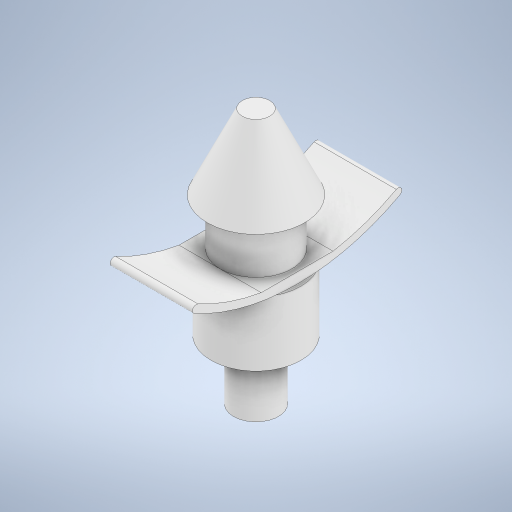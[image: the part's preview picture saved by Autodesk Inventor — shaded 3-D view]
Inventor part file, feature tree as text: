
AUTODESK INVENTOR PART (.ipt)
format: ipt  version: 2024.2 (Build 282272000, 272)  size: 308,736 bytes
history: native  units: mm
features: sketch x1, revolve x1, extrude x1, mirror x1
ambient origin geometry x8: Origin, YZ Plane, XZ Plane, XY Plane, X Axis, Y Axis, Z Axis, Center Point
bodies: Solid1 (feature_tree)
feature tree (4):
  sketch  "Sketch1"  dims[d0=3.0mm d1=4.0mm d3=6.0mm d4=5.0mm d5=6.5mm d9=8.8mm d10=4.363323mm d11=4.8mm d12=90.0deg d13=5.5mm d14=0.0mm d15=5.0mm d17=14.0mm d18=0.5mm d19=1.6mm]
  revolve  "Revolution1"  [1 undecoded]
  extrude  "Extrusion1"  Depth=14.0mm
  mirror  "Mirror1"
note: 1 required parameter value undecoded (feature->parameter linkage not recoverable at this tier; creation-order binding heuristic only, values carry confidence <= 0.55)
